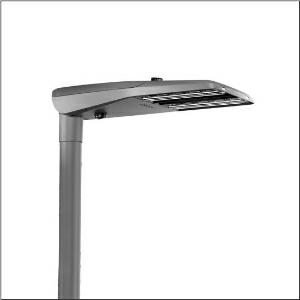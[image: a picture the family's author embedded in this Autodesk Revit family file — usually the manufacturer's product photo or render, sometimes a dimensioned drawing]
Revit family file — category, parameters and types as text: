
# Revit family: streetlight_sl_11_iq_midi___pc-r_5xc3f21y08me_3682
name_source: partatom
category: Lighting Fixtures
units: mm (PartAtom-declared; Revit-internal decimal feet)

## family parameters
Cut with Voids When Loaded = No
Host = Face
Light Source = No
Part Type = Normal
Room Calculation Point = No
Round Connector Dimension = Use Diameter
Shared = No

## types (1)
- --- (1 x LED, 12730 lm, 122.8 W, 2200K)
    Apparent Load = 123 VA
    CIE Flux Codes = 37 73 96 100 100
    Color Rendering = 70
    Color Temperature = 2200K
    Default Elevation = 1800 mm
    Description = Streetlight SL 11 iQ midi, mast luminaire, primary light control with 3 zone facetted reflector, of plastic, silver coated, highly specular, primary optical cover: cover, of PMMA, transparent, light distribution: PC-R, light emission: direct distribution, primary light characteristic: asymmetric, right, installation type: post-top, side-entry, LED, High Power LED, rated luminous flux: 12.730lm, luminous efficacy: 103lm/W, light colour: 722, colour temperature: 2200K, control: presetting dimming logarithmic, Street-Remote, Auto-Match, Temp-Guard, Lumen-Switch, Night-Set, Smart-Wire, Light-Fading, Desk-Remote (wireless, voltage-free reading and setting of iQ features in the workshop via application-optimized NFC function/RFID function), optimised constant luminous flux control (CLO 2.0), with cable H07RN-F 5x 1.5mm², mains connection: 220..240V, AC, 50/60Hz, connection cable pre-assembled, cable length: 12,5m, start of lifetime: 123W, end of service life: 130W, reduction: 56W, luminaire housing, of diecast aluminium, powder-coated, Siteco® metallic grey (DB 702S), please order mast flange separately, inclination adjustable without tools: 0°, 5°, 10°, 15° (post-top) | 0°, -5°, -10°, -15° (side-entry), sealing non-destructively replaceable, multi-level sealing system, length: 780mm, width: 376mm, height: 118mm, spigot size: 60/76mm (post-top) and 42/60/76mm (side-entry), mast flange for spigot size: 42mm: 5XC10008XM4, 60mm: 5XC10008XM2, 76/60mm: 5XC10108XM1, equipment: Power, Smart Interface below and above, protection rating (complete): IP66, insulation class (complete): insulation class II (safety insulation), certification: CE, ENEC in preparation, impact resistance: IK09, permissible operating ambient temperature for outdoor applications: -25..+50°C, standard-compliant lighting for roads and squares, packaging unit: 1 piece

Light Distribution: PC-R
    Height = 118 mm
    Lamp = 1 x LED
    Lamp Light Flux = 12730 lm
    Lamp Power = 122.8 W
    Lamp count = 1
    Length = 780 mm
    Luminous efficacy = 104 lm/W
    Manufacturer = Siteco
    ModVariant = No
    Model = 5XC3F21Y08ME
    Number of Poles = 1
    OnlyDefault = Yes
    Power Factor = 1
    Product Name = Streetlight SL 11 iQ midi | PC-R
    Product group = mast luminaire | pylon top
    ProductGroupID = 6100
    Protection Class = Protection class II
    Protection Degree = IP 66
    RLX_Detail_Level = 1
    RlxData = <blob elided: 73277 chars, md5=323b36b1>
    Socket = socket
    Standby Power = 0 W
    System Light Flux = 12729 lm
    System Power = 123 W
    Type Comments = factory setting: luminous flux: 100 % | dim-lin: 254 | 553 mA
    Type Image = l_1004429.jpg
    URL = http://relux.com
    VarID = @adj_036637
    Voltage = 0 V
    Weight = 0.00 kg
    Width = 376 mm

## geometry (parser evidence)
native form markers: Blend x4, Sweep x9
no freeform markers — native parametric forms only
